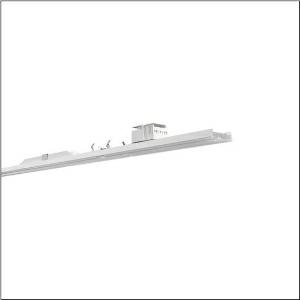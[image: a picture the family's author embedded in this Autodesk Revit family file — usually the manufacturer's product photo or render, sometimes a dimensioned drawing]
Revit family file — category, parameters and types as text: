
# Revit family: licross_r__11_recessed_mo_51tl12dn49xf3s_4535
name_source: partatom
category: Lighting Fixtures
units: mm (PartAtom-declared; Revit-internal decimal feet)

## family parameters
Cut with Voids When Loaded = No
Host = Face
Light Source = No
Part Type = Normal
Room Calculation Point = No
Round Connector Dimension = Use Diameter
Shared = No

## types (1)
- --- (1 x LED, 890 lm, 5 W, 4000K)
    Apparent Load = 5 VA
    CIE Flux Codes = 67 92 99 100 100
    Color Rendering = 80
    Color Temperature = 4000K
    Default Elevation = 1800 mm
    Description = Licross® 11 Recessed MO, luminaire insert, of sheet steel, galvanised, coil coated, white, length: 1.500mm, width: 66mm, height: 67mm, LED rated luminous flux: 9.140lm, light colour: 840, control gear: DALI 2, control gear: ECG DALI, with plug, 6-pole, with phase selection, for trunking rail, 14-core, mains connection: 220..240V, AC/DC, 0/50..60Hz, for emergency light function, halogen-free wiring, converter,control gear: single battery element, battery: LiFeP04, 9Ah, primary optical cover: cover, of PMMA, light emission: direct distribution, protection rating (complete): IP40, insulation class (complete): insulation class I (protective earthing), certification: CE, UKCA, protection symbol: D if used in an environment without relevant dust loads with corresponding accessories, permissible ambient temperature for indoor applications: +5..+35°C, standard: EN 60598-2-22, corresponds to IFS (International Featured Standards) requirements for safety and quality in the food industry, reducing of maximum allowable ambient temperature of 5°C with ceiling mounting, LABS conformity tested according to VDMA 24364:2018-05, packaging unit: 1 piece
    Height = 58 mm
    Lamp = 1 x LED
    Lamp Light Flux = 890 lm
    Lamp Power = 5 W
    Lamp count = 1
    Length = 1500 mm
    Luminous efficacy = 178 lm/W
    Manufacturer = Siteco
    ModVariant = No
    Model = 51TL12DN49XF3S
    Mounting Place = Ceiling
    Mounting Type = Pendant
    Number of Poles = 1
    OnlyDefault = Yes
    Power Factor = 1
    Product Name = Licross® 11 Recessed MO
    Product group = luminaire insert
    ProductGroupID = 902
    Protection Class = Protection class I
    Protection Degree = IP 40
    RLX_Detail_Level = 1
    RlxData = <blob elided: 22797 chars, md5=b9828ef4>
    Socket = socket
    Standby Power = 0 W
    System Light Flux = 890 lm
    System Power = 5 W
    Type Comments = : emergency light operation: 3 h
    Type Image = l_1266722.jpg
    URL = http://relux.com
    VarID = @adj_125903
    Voltage = 0 V
    Weight = 0.00 kg
    Width = 66 mm

## geometry (parser evidence)
native form markers: Blend x4, Sweep x12
no freeform markers — native parametric forms only
